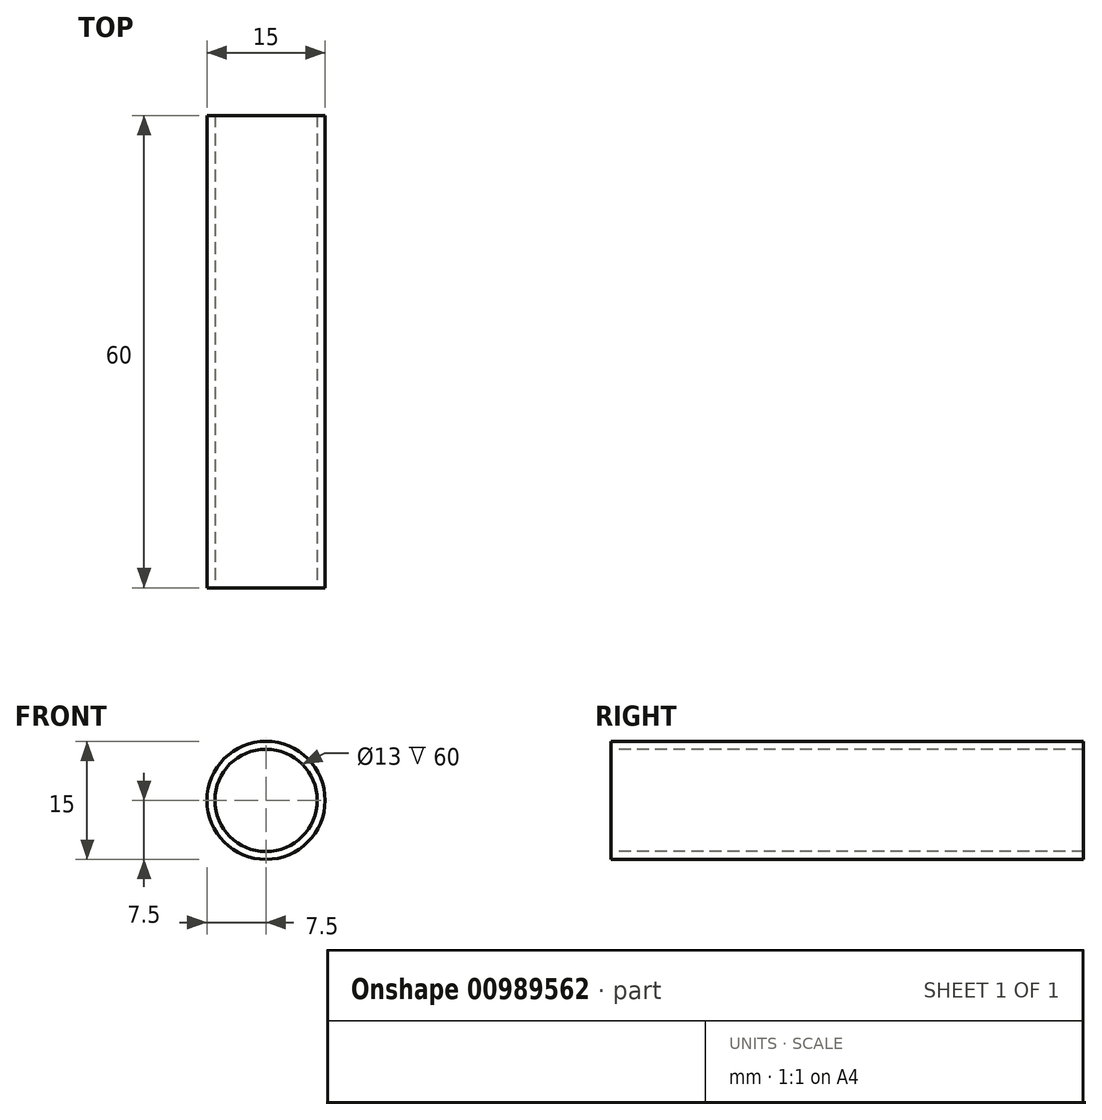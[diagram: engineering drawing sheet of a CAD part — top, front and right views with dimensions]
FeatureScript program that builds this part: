
annotation { "Feature Type Name" : "Feature", "Feature Type Description" : "" }
export const myFeature = defineFeature(function(context is Context, id is Id, definition is map)
    precondition{}
    {
        {
            var Q0;
            Q0=qCreatedBy(makeId("Front.planeOp"),FACE);
            var sketch = newSketch(context, id + "F0", { "sketchPlane" : qUnion([Q0])});
            skCircle(sketch, "E0", {"center": v(0, 0) * mm, "radius": 7.5 * mm});
            skCircle(sketch, "E1", {"center": v(0, 0) * mm, "radius": 6.5 * mm});
            skSolve(sketch);
        }
        {
            var Q0;
            Q0 = qSketchRegion(id + "F0", true);
            extrude(context, id + "F1", {"entities" : qUnion([Q0]), "oppositeDirection" : true, "depth" : 60 * mm, "offsetDistance" : 25 * mm});
        }
    });
